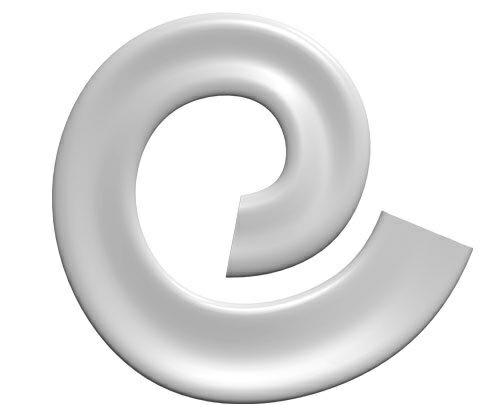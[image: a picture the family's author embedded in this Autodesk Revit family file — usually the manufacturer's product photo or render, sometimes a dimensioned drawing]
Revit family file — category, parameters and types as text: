
# Revit family: CITY ALPHABET litera „E”
name_source: partatom
category: Meble
revit_build: Autodesk Revit 2018 (Build: 20190510_1515(x64)
units: mm (PartAtom-declared; Revit-internal decimal feet)

## family parameters
Numer OmniClass = 23.40.10.11.14
Obiekt nadrzędny = Powierzchnia
Punkt obliczania pomieszczeń = Nie
Tnij formami wycięć po wczytaniu = Nie
Tytuł OmniClass = Exterior Seating
Współdzielony = Nie

## types (1)
- CITY ALPHABET litera „E”
    Domyślna rzędna = 1219 mm
    Długość = 1890 mm  [stored 6.20079 ft]
    IfcExportAs = IfcFurnishingElement
    Komentarze do typu = Ławka
    Materiał - informacja = Szeroki wybór kolorów wg palety RAL. Istnieje również możliwość specjalnego wykonania
kolorystycznego na indywidualne zapytanie klienta.
    Model = CITY ALPHABET litera „E”
    Obraz typu = E.jpg
    Producent = Astrini Design
    Szerokość = 2030 mm  [stored 6.6601 ft]
    Temepratura użytkowania = -40°C do 80°C, ( -40°F do 176°F )
    URL = http://astrini-design.pl
    Waga (szacunkowo) = 75.00 kg
    Waga po wypełnieniu (szacunkowo) = 125.00 kg
    Wysokość = 510 mm  [stored 1.67323 ft]

note: [stored X ft] marks values corroborated as IEEE doubles in the binary element streams (Revit-internal decimal feet)
